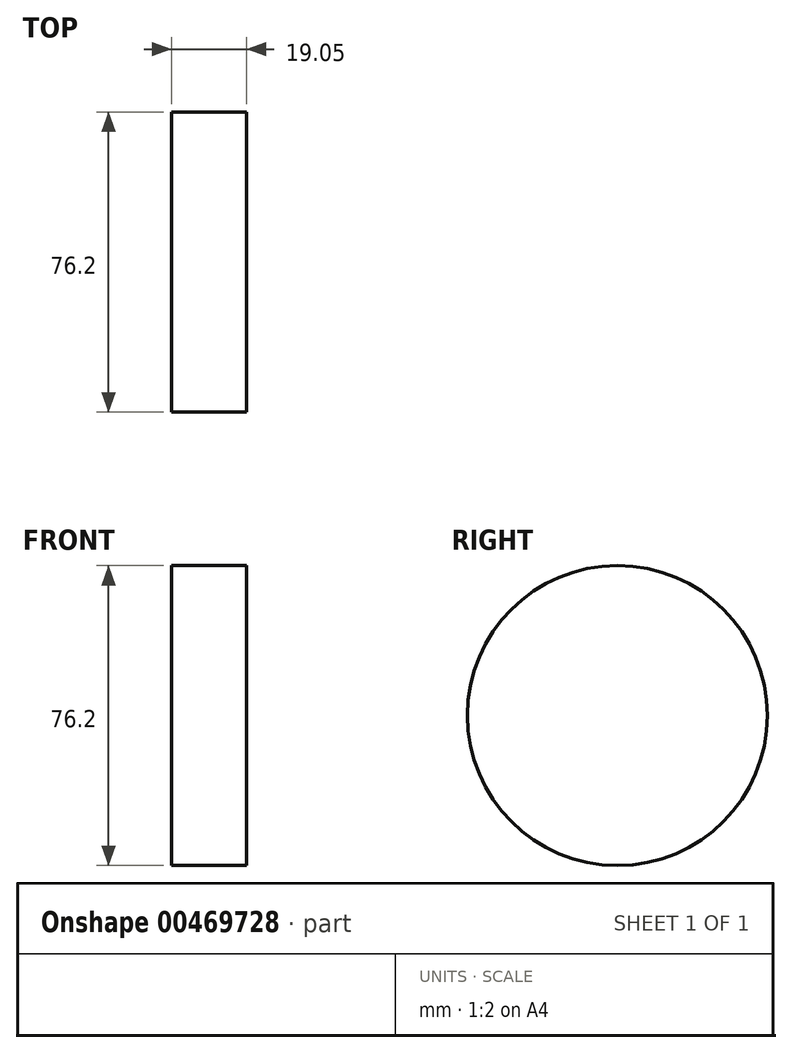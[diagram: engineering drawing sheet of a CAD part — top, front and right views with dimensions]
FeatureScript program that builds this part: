
annotation { "Feature Type Name" : "Feature", "Feature Type Description" : "" }
export const myFeature = defineFeature(function(context is Context, id is Id, definition is map)
    precondition{}
    {
        {
            var Q0;
            Q0=qCreatedBy(makeId("Right.planeOp"),FACE);
            var sketch = newSketch(context, id + "F0", { "sketchPlane" : qUnion([Q0])});
            skCircle(sketch, "E0", {"center": v(0, 0) * mm, "radius": 38.1 * mm});
            skSolve(sketch);
        }
        {
            var Q0;
            Q0=makeQuery(id+"F0.imprint","IMPRINT",FACE,{"disambiguationData":[TD([[makeQuery(id+"F0.imprint","IMPRINT",EDGE,{"derivedFrom":sQuery(id+"F0.wireOp",EDGE,"E0")}),1.0]])]});
            extrude(context, id + "F1", {"entities" : qUnion([Q0]), "depth" : 19.05 * mm, "offsetDistance" : 25.4 * mm});
        }
    });
